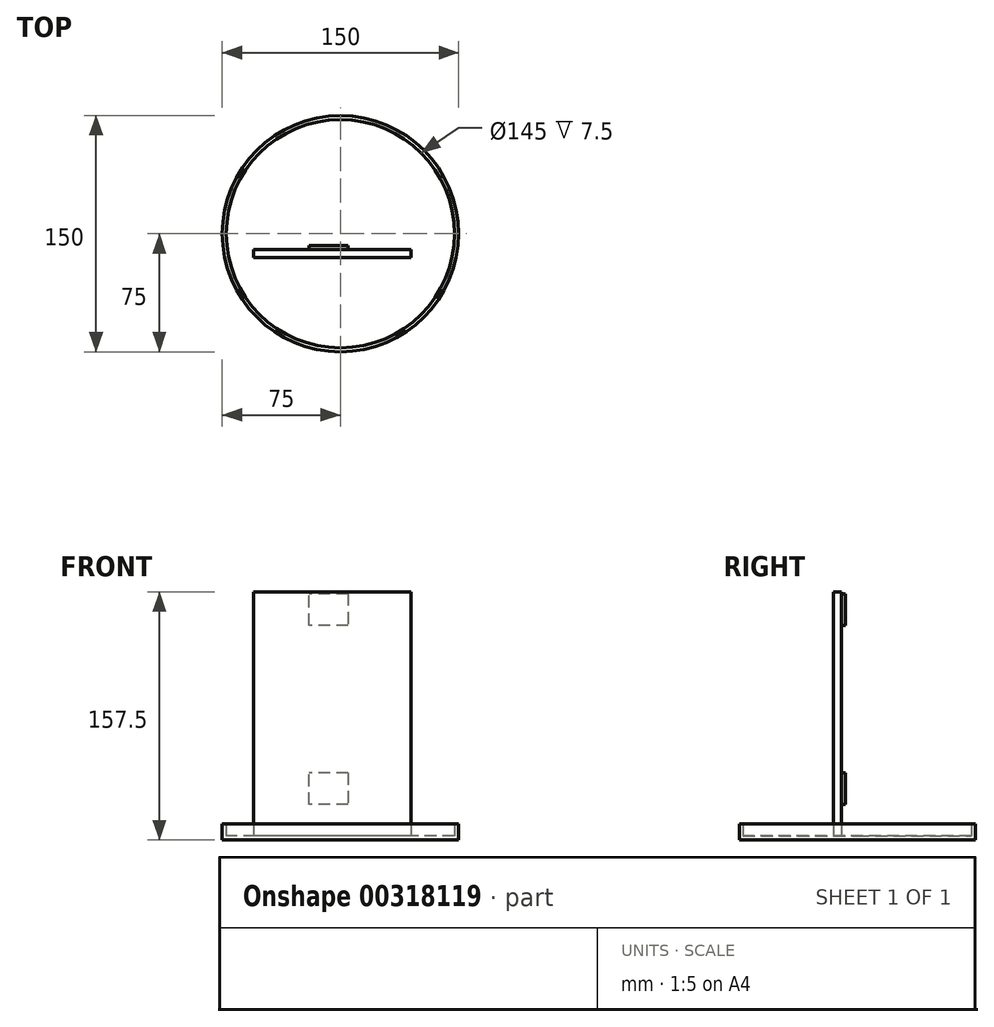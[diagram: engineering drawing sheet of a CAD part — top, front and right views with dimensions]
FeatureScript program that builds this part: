
annotation { "Feature Type Name" : "Feature", "Feature Type Description" : "" }
export const myFeature = defineFeature(function(context is Context, id is Id, definition is map)
    precondition{}
    {
        {
            var Q0;
            Q0=qCreatedBy(makeId("Top.planeOp"),FACE);
            var sketch = newSketch(context, id + "F0", { "sketchPlane" : qUnion([Q0])});
            skCircle(sketch, "E0", {"center": v(0, 0) * mm, "radius": 72.5 * mm});
            skCircle(sketch, "E1", {"center": v(0, 0) * mm, "radius": 75 * mm});
            skSolve(sketch);
        }
        {
            var Q0;
            Q0=qSketchRegion(id+"F0",true);
            extrude(context, id + "F1", {"entities" : qUnion([Q0]), "depth" : 10 * mm});
        }
        {
            var Q0;
            Q0=makeQuery(id+"F0.imprint","IMPRINT",FACE,{"disambiguationData":[TD([[makeQuery(id+"F0.imprint","IMPRINT",EDGE,{"derivedFrom":sQuery(id+"F0.wireOp",EDGE,"E0")}),1.0]])]});
            extrude(context, id + "F2", {"entities" : qUnion([Q0]), "operationType" : NewBodyOperationType.ADD, "depth" : 2.5 * mm});
        }
        {
            var Q0;
            Q0=makeQuery(id+"F2.opExtrude","CAP_FACE",FACE,{"disambiguationData":[OSD([sQuery(id+"F0.wireOp",EDGE,"E0")])],"isStart":false});
            var sketch = newSketch(context, id + "F3", { "sketchPlane" : qUnion([Q0])});
            skLineSegment(sketch, "E2", {"start": v(45, -10) * mm, "end": v(-55, -10) * mm});
            skLineSegment(sketch, "E3", {"start": v(-55, -15) * mm, "end": v(-55, -10) * mm});
            skLineSegment(sketch, "E4", {"start": v(-55, -15) * mm, "end": v(45, -15) * mm});
            skLineSegment(sketch, "E5", {"start": v(45, -15) * mm, "end": v(45, -10) * mm});
            skSolve(sketch);
        }
        {
            var Q0;
            Q0=qSketchRegion(id+"F3",true);
            extrude(context, id + "F4", {"entities" : qUnion([Q0]), "operationType" : NewBodyOperationType.ADD, "depth" : 155 * mm});
        }
        {
            var Q0;
            Q0=makeQuery(id+"F4.opExtrude","SWEPT_FACE",FACE,{"disambiguationData":[OSD([sQuery(id+"F3.wireOp",EDGE,"E2")])]});
            var sketch = newSketch(context, id + "F5", { "sketchPlane" : qUnion([Q0])});
            skLineSegment(sketch, "E6", {"start": v(-5, 42.5) * mm, "end": v(20, 42.5) * mm});
            skLineSegment(sketch, "E7", {"start": v(-5, 42.5) * mm, "end": v(-5, 22.5) * mm});
            skLineSegment(sketch, "E8", {"start": v(-5, 22.5) * mm, "end": v(20, 22.5) * mm});
            skLineSegment(sketch, "E9", {"start": v(20, 22.5) * mm, "end": v(20, 42.5) * mm});
            skSolve(sketch);
        }
        {
            var Q0;
            Q0=qSketchRegion(id+"F5",true);
            extrude(context, id + "F6", {"entities" : qUnion([Q0]), "operationType" : NewBodyOperationType.ADD, "depth" : 2.5 * mm});
        }
        {
            var Q0;
            Q0=makeQuery(id+"F4.opExtrude","SWEPT_FACE",FACE,{"disambiguationData":[OSD([sQuery(id+"F3.wireOp",EDGE,"E2")])]});
            var sketch = newSketch(context, id + "F7", { "sketchPlane" : qUnion([Q0])});
            skLineSegment(sketch, "E10", {"start": v(-45, 157.5) * mm, "end": v(-5, 157.5) * mm});
            skLineSegment(sketch, "E11", {"start": v(-5, 157.5) * mm, "end": v(-5, 156.25) * mm});
            skLineSegment(sketch, "E12", {"start": v(-5, 156.25) * mm, "end": v(20, 156.25) * mm});
            skLineSegment(sketch, "E13", {"start": v(-5, 156.25) * mm, "end": v(-5, 136.25) * mm});
            skLineSegment(sketch, "E14", {"start": v(-5, 136.25) * mm, "end": v(20, 136.25) * mm});
            skLineSegment(sketch, "E15", {"start": v(20, 136.25) * mm, "end": v(20, 156.25) * mm});
            skSolve(sketch);
        }
        {
            var Q0;
            Q0=qSketchRegion(id+"F7",true);
            extrude(context, id + "F8", {"entities" : qUnion([Q0]), "operationType" : NewBodyOperationType.ADD, "depth" : 2.5 * mm});
        }
    });
